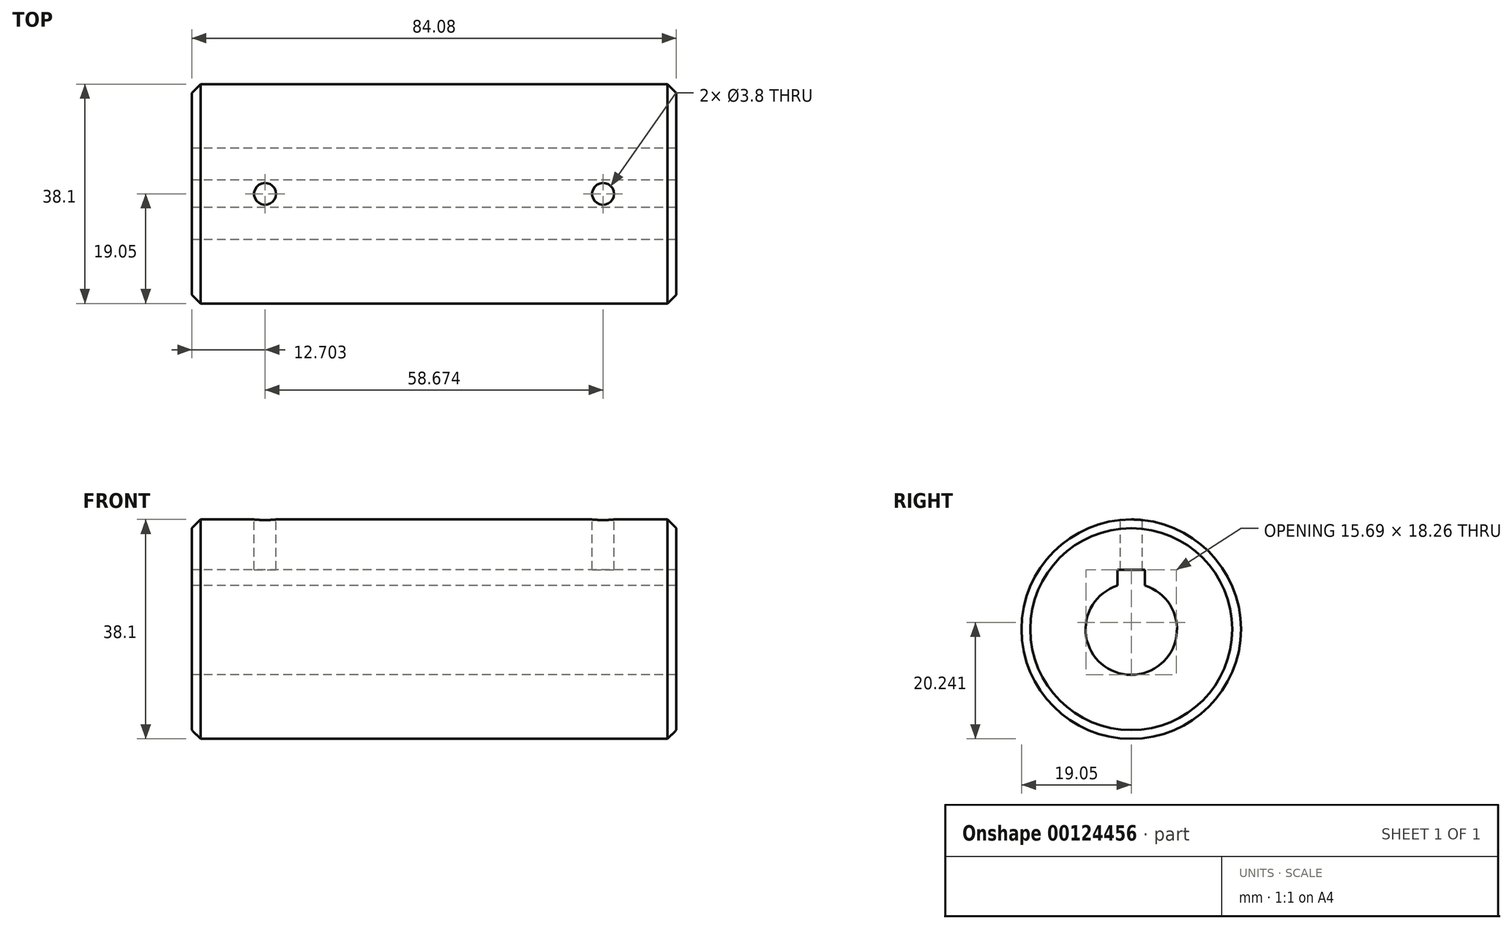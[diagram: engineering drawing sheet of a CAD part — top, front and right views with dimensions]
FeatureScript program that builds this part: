
annotation { "Feature Type Name" : "Feature", "Feature Type Description" : "" }
export const myFeature = defineFeature(function(context is Context, id is Id, definition is map)
    precondition{}
    {
        {
            var Q0;
            Q0=qCreatedBy(makeId("Right.planeOp"),FACE);
            var sketch = newSketch(context, id + "F0", { "sketchPlane" : qUnion([Q0])});
            skCircle(sketch, "E0", {"center": v(0, 0) * mm, "radius": 19.05 * mm});
            skArc(sketch, "E1", {"start": v(-2.38, 7.57) * mm, "mid": v(0, -7.94) * mm, "end": v(2.38, 7.57) * mm});
            skLineSegment(sketch, "E2", {"start": v(0, 0) * mm, "end": v(0, 7.94) * mm, "construction": true});
            skLineSegment(sketch, "E3.0", {"start": v(2.38, 0) * mm, "end": v(2.38, 2.77) * mm, "construction": true});
            skLineSegment(sketch, "E4", {"start": v(2.38, 7.94) * mm, "end": v(0, 7.94) * mm, "construction": true});
            skLineSegment(sketch, "E5.0", {"start": v(2.38, 10.32) * mm, "end": v(0, 10.32) * mm, "construction": true});
            skLineSegment(sketch, "E6.bottom", {"start": v(2.38, 10.32) * mm, "end": v(-2.38, 10.32) * mm});
            skLineSegment(sketch, "E6.top", {"start": v(2.38, 2.77) * mm, "end": v(0, 2.77) * mm});
            skLineSegment(sketch, "E6.left", {"start": v(2.38, 10.32) * mm, "end": v(2.38, 7.57) * mm});
            skLineSegment(sketch, "E6.right", {"start": v(-2.38, 10.32) * mm, "end": v(-2.38, 7.57) * mm});
            skLineSegment(sketch, "E7.trimOffspring", {"start": v(2.38, 7.57) * mm, "end": v(2.38, 7.94) * mm, "construction": true});
            skSolve(sketch);
        }
        {
            var Q0;
            Q0 = qSketchRegion(id + "F0", true);
            extrude(context, id + "F1", {"entities" : qUnion([Q0]), "endBound" : BoundingType.SYMMETRIC, "depth" : 84.07 * mm});
        }
        {
            var Q0;
            Q0=qCreatedBy(makeId("Top.planeOp"),FACE);
            cPlane(context, id + "F2", {"entities" : qUnion([Q0]), "cplaneType" : CPlaneType.OFFSET, "offset" : 19.05 * mm, "width" : 152.4 * mm, "height" : 152.4 * mm});
        }
        {
            var Q0;
            Q0=qCreatedBy(id+"F2.planeOp",FACE);
            var sketch = newSketch(context, id + "F3", { "sketchPlane" : qUnion([Q0])});
            skLineSegment(sketch, "E8.0", {"start": v(42.04, 19.05) * mm, "end": v(42.04, -19.05) * mm, "construction": true});
            skLineSegment(sketch, "E9.0", {"start": v(-42.04, 19.05) * mm, "end": v(-42.04, -19.05) * mm, "construction": true});
            skLineSegment(sketch, "E10", {"start": v(-42.04, 0) * mm, "end": v(42.04, 0) * mm, "construction": true});
            skLineSegment(sketch, "E11.0", {"start": v(-29.34, 19.05) * mm, "end": v(-29.34, -19.05) * mm, "construction": true});
            skLineSegment(sketch, "E12.0", {"start": v(29.34, 19.05) * mm, "end": v(29.34, -19.05) * mm, "construction": true});
            skPoint(sketch, "E13", {"position": v(-29.34, 0) * mm});
            skPoint(sketch, "E14", {"position": v(29.34, 0) * mm});
            skSolve(sketch);
        }
        {
            var Q0;
            Q0=sQuery(id+"F3.wireOp",VERTEX,"E14");
            var Q1;
            Q1=sQuery(id+"F3.wireOp",VERTEX,"E13");
            var Q2;
            Q2=makeQuery(id+"F1.opExtrude","SWEPT_BODY",BODY,{"disambiguationData":[OSD([sQuery(id+"F0.wireOp",EDGE,"E0"),sQuery(id+"F0.wireOp",EDGE,"E1"),sQuery(id+"F0.wireOp",EDGE,"E6.bottom"),sQuery(id+"F0.wireOp",EDGE,"E6.left"),sQuery(id+"F0.wireOp",EDGE,"E6.right")])]});
            hole(context, id + "F4", {"style" : HoleStyle.SIMPLE, "endStyle" : HoleEndStyle.BLIND, "standardTappedOrClearance" : lookupTablePath({ "standard" : "ANSI", "engagement" : "75%", "pitch" : "24 tpi", "size" : "#10", "type" : "Tapped" }), "standardBlindInLast" : lookupTablePath({ "standard" : "ANSI", "engagement" : "75%", "pitch" : "24 tpi", "size" : "#10", "type" : "Tapped" }), "holeDiameter" : 3.8 * mm, "holeDepth" : 12 * mm, "locations" : qUnion([Q0, Q1]), "scope" : qUnion([Q2]), "majorDiameter" : 4.83 * mm});
        }
        {
            var Q0;
            Q0=makeQuery(id+"F1.opExtrude","CAP_EDGE",EDGE,{"disambiguationData":[OSD([sQuery(id+"F0.wireOp",EDGE,"E0")])],"isStart":false});
            var Q1;
            Q1=makeQuery(id+"F1.opExtrude","CAP_EDGE",EDGE,{"disambiguationData":[OSD([sQuery(id+"F0.wireOp",EDGE,"E0")])],"isStart":true});
            chamfer(context, id + "F5", {"entities" : qUnion([Q0, Q1]), "width" : 1.52 * mm, "tangentPropagation" : true});
        }
    });
